# Revit family: PRD_AR_TltRllHldrs_EXOSJumboToiletRollHolder_EXOS670X
name_source: partatom
category: Specialty Equipment
revit_build: Autodesk Revit 2018 (Build: 20190510_1515(x64)
units: mm (PartAtom-declared; Revit-internal decimal feet)

## family parameters
Cut with Voids When Loaded = No
Host = Face
OmniClass Number = 23.40.20.21.21
OmniClass Title = Toilet Paper Dispensers
Part Type = Normal
Room Calculation Point = No
Round Connector Dimension = Use Diameter
Shared = No

## types (1)
- EXOS670X
    AssetType = Fixed
    BIMObjectName = PRD_AR_ToiletRollHolders_EXOSJumboToiletRollHolder_EXOS670X
    Category = Pr_40_20_76_88, Toilet roll holders
    Default Elevation = 900 mm  [stored 2.95276 ft]
    Description = Jumbo toilet roll holder for wall mounting, chromium nickel steel, with satin-finish and InoxPlus surface refinement for the reduction of finger marks making it easier to clean. Material thickness 1.2 mm, closed casing with inspection windows on the side, paper dispensed over two serrated tear-off edges, cylinder lock with KWC standard key, for one jumbo roll with a maximum diameter of 280 mm and a tube measuring 40 mm, includes mounting materials.
    DispenserMaterial = PRD_AR_StainlessSteel_SatinFinished
    DurationUnit = year
    Features = stainless steel, surface satin finished
    FillingQuantity = 1
    FillingQuantityUom = Rolls
    Finish = satin finished
    GrossWeight = 5.79 kg
    IfcExportAs = IfcFurnitureType
    IfcExportType = USERDEFINED
    IntegralAccessories = incl. mounting materials
    IsBuiltIn = TRUE
    Lock = Key-lock
    MainColor = stainless steel
    Manufacturer = KWC Group AG
    ManufacturerName = KWC Group AG
    ManufacturerURL = www.kwc.com
    Material = stainless steel
    MaterialCode = 1.4301
    MaterialThickness = 1.20 mm
    MaximumDepthDiameterOfConsumable = 295.00 mm
    MaximumWidthOfConsumable = 105.00 mm
    Model = EXOS670X
    ModelNumber = 2030028245
    ModelReference = EXOS670X
    NBSDescription = Toilet roll holders
    NBSReference = 45-35-72/368
    Name = Jumbo toilet roll holder EXOS670X
    NetWeight = 4.40 kg
    NominalDepth = 130 mm  [stored 0.426509 ft]
    NominalHeight = 364 mm  [stored 1.19423 ft]
    NominalWidth = 325 mm  [stored 1.06627 ft]
    PanelMaterial = PRD_AR_StainlessSteel_SatinFinished
    ProductInformation = https://pim.kwc.com
    Size = 325 x 364 x 130 mm
    Spindle = Yes
    Style = Roll holder
    SurfaceTreatment = InoxPlus (anti fingerprint)
    ToiletRollMaterial = PRD_AR_ToiletRoll
    TypeOfFixing = Screw
    TypeOfMounting = Wall mounting
    URL = www.kwc.com
    Uniclass2015Code = Pr_40_20_76_88
    Uniclass2015Title = Toilet roll holders
    Uniclass2015Version = Products v1.17
    Version = 1
    WarrantyDurationUnit = year

note: [stored X ft] marks values corroborated as IEEE doubles in the binary element streams (Revit-internal decimal feet)

## geometry (parser evidence)
native form markers: Sweep x5
no freeform markers — native parametric forms only
